# Revit family: LAMP_KOMBIC 100 ROUND IP40 TW OPTIC
name_source: partatom
category: Luminarias
revit_build: Autodesk Revit 2018 (Build: 20190510_1515(x64)
units: mm (PartAtom-declared; Revit-internal decimal feet)

## family parameters
Anfitrión = Cara
Compartido = No
Corte con vacíos al cargar = No
Cota de conector redondo = Diámetro de uso
Origen de luz = Sí
Punto de cálculo de habitación = No
Tipo de pieza = Normal

## types (4) — shared parameters
CRI = 90
Cambio de temperatura de color de luz atenuada = <Ninguno>
Diameter = 99 mm  [stored 0.324803 ft]
Elevación por defecto = 1219 mm
Fabricante = LAMP
Filtro de color = 16777215
Gear = Electronic
Height = 75 mm
IEE = A
Initial color = 2700-5000K
Installation instructions = https://www.lamp.es
Insulation class = II
LED Lifetime = 70.000 L80 B10
Lamp = HIGH POWER LED
Last update = 19/07/2021
Luminaire type = Downlight
MacAdam = 3
Manufacturer URL = http://www.lamp.es
Manufacturer country = Spain
Manufacturer name = LAMP
Material COB = LAMP_COB
Material difusor = LAMP_PMMA Difusor Kombic
Material disipador = LAMP_Aluminio Disipador Kombic
Material optica = LAMP_PMMA Optica Kombic100
Plum = 21 W
Power = 16 W
Power Supply = 220-240V 50/60Hz
Product URL = https://www.lamp.es
Product datasheet = http://www.lamp.es
Protection rating = IP40
Recessed diameter = 95 mm
Type = BRIDGELUX
Weight = 0.55 kg
Ángulo de inclinación = -90.00°

## per-type parameters (varying)
| type | Archivo de red fotométrica | Efficacy | Finish | Material aro | Material reflector | Modelo | Product code |
| 1001LM TW DALI B/B | K11RD2040WF9TWDBB.IES | 48 lm/W | #N/A | LAMP_Plástico genérico NG | LAMP_PC Reflector Kombic Metalizado Negro | K11RD2040WF9TWDBB | K11RD2040WF9TWDBB |
| 1001LM TW DALI B/W | K11RD2040WF9TWDBW.IES | 48 lm/W | Shiny white RAL 9010 | LAMP_Plástico genérico BL | LAMP_PC Reflector Kombic Metalizado Negro | K11RD2040WF9TWDBW | K11RD2040WF9TWDBW |
| 1050LM TW DALI M/W | K11RD2040WF9TWDMW.IES | 51 lm/W | Shiny white RAL 9010 | LAMP_Plástico genérico BL | LAMP_PC Reflector Kombic Metalizado Mate | K11RD2040WF9TWDMW | K11RD2040WF9TWDMW |
| 1050LM TW DALI W/W | K11RD2040WF9TWDWW.IES | 51 lm/W | Matte white RAL 9010 | LAMP_Plástico genérico BL | LAMP_PC Reflector Kombic Blanco | K11RD2040WF9TWDWW | K11RD2040WF9TWDWW |

note: [stored X ft] marks values corroborated as IEEE doubles in the binary element streams (Revit-internal decimal feet)
